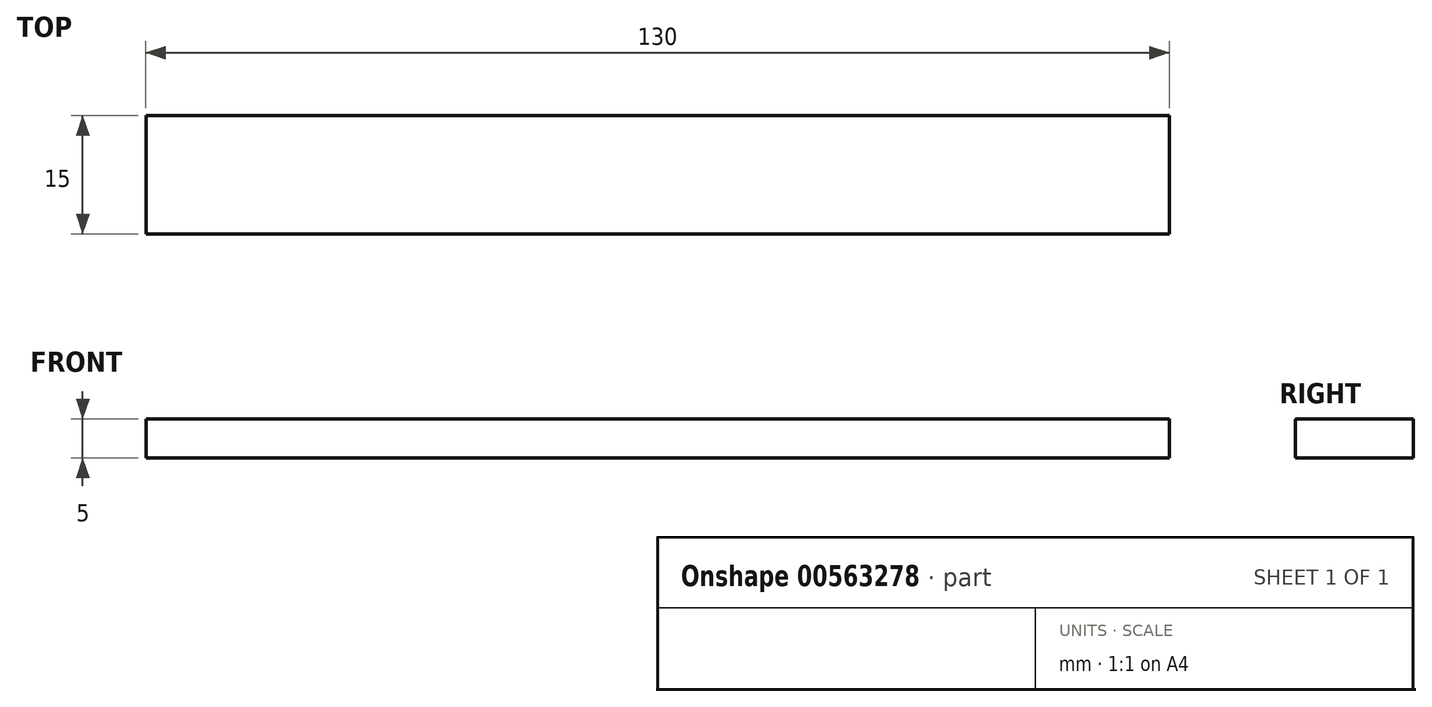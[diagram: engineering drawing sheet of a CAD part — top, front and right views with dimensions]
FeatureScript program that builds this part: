
annotation { "Feature Type Name" : "Feature", "Feature Type Description" : "" }
export const myFeature = defineFeature(function(context is Context, id is Id, definition is map)
    precondition{}
    {
        {
            var Q0;
            Q0=qCreatedBy(makeId("Top.planeOp"),FACE);
            var sketch = newSketch(context, id + "F0", { "sketchPlane" : qUnion([Q0])});
            skLineSegment(sketch, "E0.bottom", {"start": v(86.23, 0) * mm, "end": v(-43.77, 0) * mm});
            skLineSegment(sketch, "E0.top", {"start": v(86.23, 15) * mm, "end": v(-43.77, 15) * mm});
            skLineSegment(sketch, "E0.left", {"start": v(86.23, 0) * mm, "end": v(86.23, 15) * mm});
            skLineSegment(sketch, "E0.right", {"start": v(-43.77, 0) * mm, "end": v(-43.77, 15) * mm});
            skSolve(sketch);
        }
        {
            var Q0;
            Q0 = qSketchRegion(id + "F0", true);
            extrude(context, id + "F1", {"entities" : qUnion([Q0]), "depth" : 5 * mm, "offsetDistance" : 25 * mm});
        }
    });
